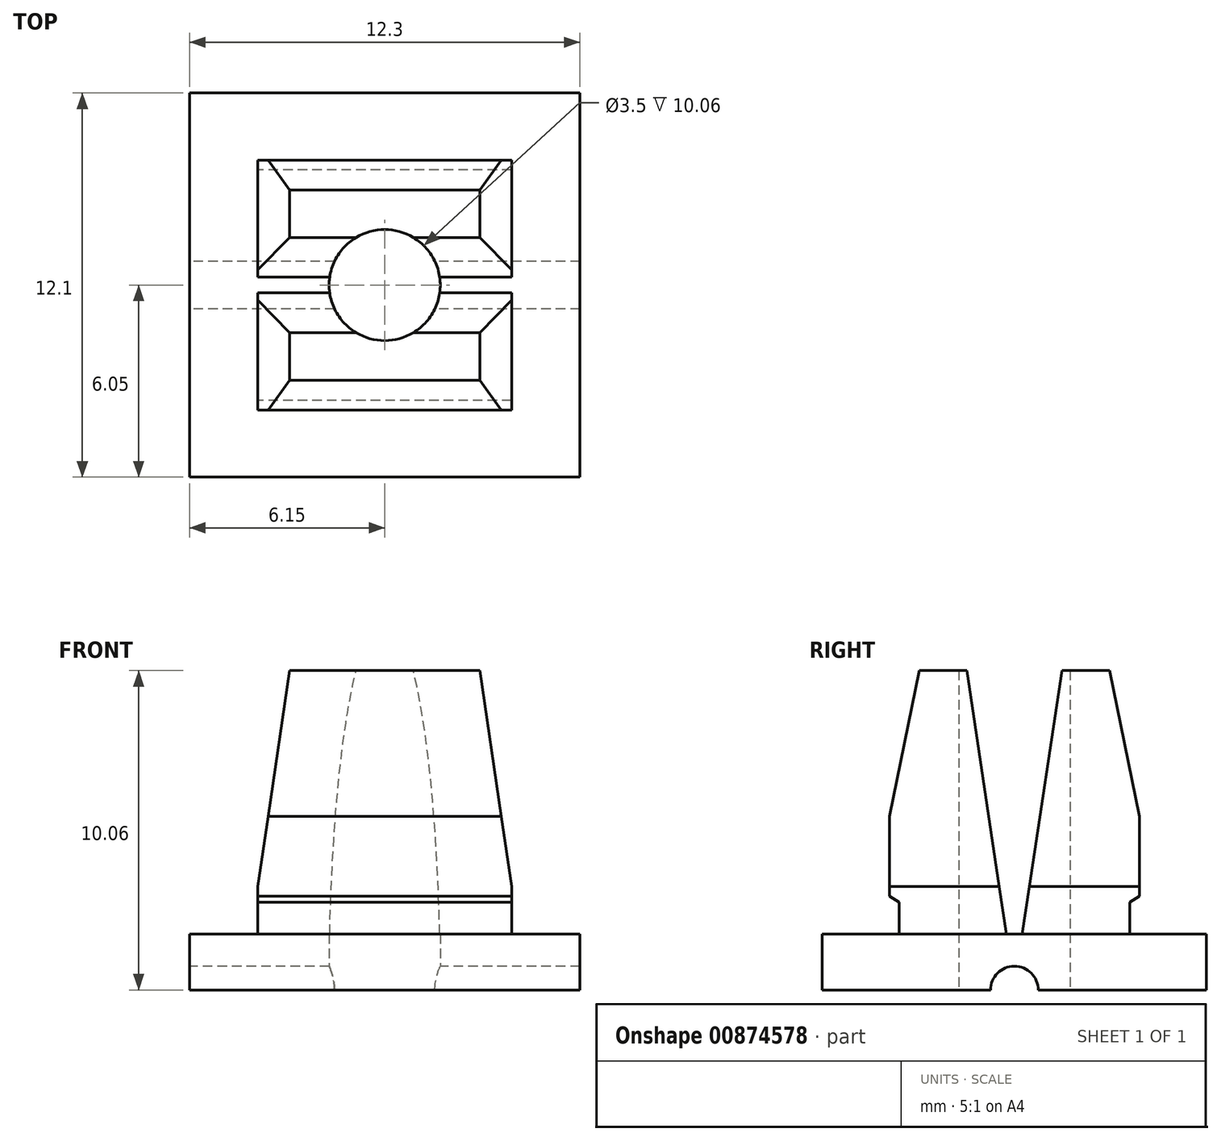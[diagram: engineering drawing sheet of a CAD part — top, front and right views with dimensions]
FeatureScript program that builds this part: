
annotation { "Feature Type Name" : "Feature", "Feature Type Description" : "" }
export const myFeature = defineFeature(function(context is Context, id is Id, definition is map)
    precondition{}
    {
        {
            var Q0;
            Q0=qCreatedBy(makeId("Top.planeOp"),FACE);
            var sketch = newSketch(context, id + "F0", { "sketchPlane" : qUnion([Q0])});
            skLineSegment(sketch, "E0.bottom", {"start": v(-12.3, 12.1) * mm, "end": v(0, 12.1) * mm});
            skLineSegment(sketch, "E0.top", {"start": v(-12.3, 0) * mm, "end": v(0, 0) * mm});
            skLineSegment(sketch, "E0.left", {"start": v(-12.3, 12.1) * mm, "end": v(-12.3, 0) * mm});
            skLineSegment(sketch, "E0.right", {"start": v(0, 12.1) * mm, "end": v(0, 0) * mm});
            skSolve(sketch);
        }
        {
            var Q0;
            Q0=makeQuery(id+"F0.imprint","IMPRINT",FACE,{"disambiguationData":[TD([[makeQuery(id+"F0.imprint","IMPRINT",EDGE,{"derivedFrom":sQuery(id+"F0.wireOp",EDGE,"E0.bottom")}),-1.0]])]});
            extrude(context, id + "F1", {"entities" : qUnion([Q0]), "depth" : 1.76 * mm, "offsetDistance" : 25 * mm});
        }
        {
            var Q0;
            Q0=makeQuery(id+"F1.opExtrude","CAP_FACE",FACE,{"disambiguationData":[OSD([sQuery(id+"F0.wireOp",EDGE,"E0.bottom"),sQuery(id+"F0.wireOp",EDGE,"E0.top"),sQuery(id+"F0.wireOp",EDGE,"E0.left"),sQuery(id+"F0.wireOp",EDGE,"E0.right")])],"isStart":false});
            var sketch = newSketch(context, id + "F2", { "sketchPlane" : qUnion([Q0])});
            skLineSegment(sketch, "E1", {"start": v(-12.3, 0) * mm, "end": v(0, 12.1) * mm, "construction": true});
            skLineSegment(sketch, "E2.bottom", {"start": v(-2.15, 9.98) * mm, "end": v(-10.15, 9.98) * mm});
            skLineSegment(sketch, "E2.top", {"start": v(-2.15, 2.12) * mm, "end": v(-10.15, 2.12) * mm});
            skLineSegment(sketch, "E2.left", {"start": v(-2.15, 9.98) * mm, "end": v(-2.15, 2.12) * mm});
            skLineSegment(sketch, "E2.right", {"start": v(-10.15, 9.98) * mm, "end": v(-10.15, 2.12) * mm});
            skLineSegment(sketch, "E3", {"start": v(-12.3, 12.1) * mm, "end": v(0, 0) * mm, "construction": true});
            skLineSegment(sketch, "E4.bottom", {"start": v(-10.15, 9.98) * mm, "end": v(-2.15, 9.98) * mm});
            skLineSegment(sketch, "E4.top", {"start": v(-10.15, 10.43) * mm, "end": v(-2.15, 10.43) * mm});
            skLineSegment(sketch, "E4.left", {"start": v(-10.15, 9.98) * mm, "end": v(-10.15, 10.43) * mm});
            skLineSegment(sketch, "E4.right", {"start": v(-2.15, 9.98) * mm, "end": v(-2.15, 10.43) * mm});
            skLineSegment(sketch, "E5.bottom", {"start": v(-10.15, 2.12) * mm, "end": v(-2.15, 2.12) * mm});
            skLineSegment(sketch, "E5.top", {"start": v(-10.15, 1.67) * mm, "end": v(-2.15, 1.67) * mm});
            skLineSegment(sketch, "E5.left", {"start": v(-10.15, 2.12) * mm, "end": v(-10.15, 1.67) * mm});
            skLineSegment(sketch, "E5.right", {"start": v(-2.15, 2.12) * mm, "end": v(-2.15, 1.67) * mm});
            skSolve(sketch);
        }
        {
            var Q0;
            Q0=makeQuery(id+"F2.imprint","IMPRINT",FACE,{"disambiguationData":[TD([[makeQuery(id+"F2.imprint","IMPRINT",EDGE,{"derivedFrom":sQuery(id+"F2.wireOp",EDGE,"E4.bottom")}),1.0]])]});
            var Q1;
            Q1=makeQuery(id+"F2.imprint","IMPRINT",FACE,{"disambiguationData":[TD([[makeQuery(id+"F2.imprint","IMPRINT",EDGE,{"derivedFrom":sQuery(id+"F2.wireOp",EDGE,"E2.left")}),-1.0]])]});
            var Q2;
            Q2=makeQuery(id+"F2.imprint","IMPRINT",FACE,{"disambiguationData":[TD([[makeQuery(id+"F2.imprint","IMPRINT",EDGE,{"derivedFrom":sQuery(id+"F2.wireOp",EDGE,"E5.bottom")}),-1.0]])]});
            extrude(context, id + "F3", {"entities" : qUnion([Q0, Q1, Q2]), "operationType" : NewBodyOperationType.ADD, "depth" : 8.3 * mm, "offsetDistance" : 25 * mm});
        }
        {
            var Q0;
            Q0=makeQuery(id+"F3.opExtrude","SWEPT_FACE",FACE,{"disambiguationData":[OSD([sQuery(id+"F2.wireOp",EDGE,"E2.right"),sQuery(id+"F2.wireOp",EDGE,"E4.left"),sQuery(id+"F2.wireOp",EDGE,"E5.left")])]});
            var sketch = newSketch(context, id + "F4", { "sketchPlane" : qUnion([Q0])});
            skLineSegment(sketch, "E6", {"start": v(-7.55, 10.06) * mm, "end": v(-6.3, 1.76) * mm});
            skLineSegment(sketch, "E7", {"start": v(-5.8, 1.76) * mm, "end": v(-4.55, 10.06) * mm});
            skLineSegment(sketch, "E8", {"start": v(-10.43, 3.26) * mm, "end": v(-9.05, 10.06) * mm});
            skLineSegment(sketch, "E9", {"start": v(-1.67, 3.26) * mm, "end": v(-3.05, 10.06) * mm});
            skLineSegment(sketch, "E10", {"start": v(-10.43, 3.26) * mm, "end": v(-9.68, 2.76) * mm});
            skLineSegment(sketch, "E11", {"start": v(-9.68, 2.76) * mm, "end": v(-9.68, 1.76) * mm});
            skLineSegment(sketch, "E12", {"start": v(-1.67, 3.26) * mm, "end": v(-2.42, 2.76) * mm});
            skLineSegment(sketch, "E13", {"start": v(-2.42, 2.76) * mm, "end": v(-2.42, 1.76) * mm});
            skLineSegment(sketch, "E14", {"start": v(-5.8, 1.76) * mm, "end": v(-6.3, 1.76) * mm});
            skSolve(sketch);
        }
        {
            var Q0;
            {var subQ0=sQuery(id+"F4.wireOp",EDGE,"E8");Q0=makeQuery(id+"F4.imprint","IMPRINT",FACE,{"disambiguationData":[TD([[makeQuery(id+"F4.imprint","IMPRINT",EDGE,{"derivedFrom":subQ0}),1.0]])]});}
            var Q1;
            {var subQ0=sQuery(id+"F4.wireOp",EDGE,"E6");Q1=makeQuery(id+"F4.imprint","IMPRINT",FACE,{"disambiguationData":[TD([[makeQuery(id+"F4.imprint","IMPRINT",EDGE,{"derivedFrom":subQ0}),1.0]])]});}
            var Q2;
            {var subQ0=sQuery(id+"F4.wireOp",EDGE,"E9");Q2=makeQuery(id+"F4.imprint","IMPRINT",FACE,{"disambiguationData":[TD([[makeQuery(id+"F4.imprint","IMPRINT",EDGE,{"derivedFrom":subQ0}),-1.0]])]});}
            var Q3;
            {var subQ0=sQuery(id+"F4.wireOp",EDGE,"E10");Q3=makeQuery(id+"F4.imprint","IMPRINT",FACE,{"disambiguationData":[TD([[makeQuery(id+"F4.imprint","IMPRINT",EDGE,{"derivedFrom":subQ0}),-1.0]])]});}
            var Q4;
            {var subQ0=sQuery(id+"F4.wireOp",EDGE,"E12");Q4=makeQuery(id+"F4.imprint","IMPRINT",FACE,{"disambiguationData":[TD([[makeQuery(id+"F4.imprint","IMPRINT",EDGE,{"derivedFrom":subQ0}),1.0]])]});}
            extrude(context, id + "F5", {"entities" : qUnion([Q0, Q1, Q2, Q3, Q4]), "operationType" : NewBodyOperationType.REMOVE, "endBound" : BoundingType.THROUGH_ALL, "oppositeDirection" : true, "depth" : 25 * mm, "offsetDistance" : 25 * mm});
        }
        {
            var Q0;
            Q0=qCreatedBy(makeId("Front.planeOp"),FACE);
            var sketch = newSketch(context, id + "F6", { "sketchPlane" : qUnion([Q0])});
            skLineSegment(sketch, "E15.0", {"start": v(-2.15, 10.06) * mm, "end": v(-10.15, 10.06) * mm, "construction": true});
            skLineSegment(sketch, "E16.0", {"start": v(-10.15, 3.26) * mm, "end": v(-10.15, 10.06) * mm});
            skLineSegment(sketch, "E17.0", {"start": v(-2.15, 3.26) * mm, "end": v(-2.15, 10.06) * mm});
            skLineSegment(sketch, "E18", {"start": v(-9.15, 10.06) * mm, "end": v(-10.15, 3.26) * mm});
            skLineSegment(sketch, "E19", {"start": v(-3.15, 10.06) * mm, "end": v(-2.15, 3.26) * mm});
            skPoint(sketch, "E20", {"position": v(-6.15, 10.06) * mm});
            skLineSegment(sketch, "E21", {"start": v(-10.15, 10.06) * mm, "end": v(-9.15, 10.06) * mm});
            skLineSegment(sketch, "E22", {"start": v(-3.15, 10.06) * mm, "end": v(-2.15, 10.06) * mm});
            skSolve(sketch);
        }
        {
            var Q0;
            Q0=makeQuery(id+"F6.imprint","IMPRINT",FACE,{"disambiguationData":[TD([[makeQuery(id+"F6.imprint","IMPRINT",EDGE,{"derivedFrom":sQuery(id+"F6.wireOp",EDGE,"E16.0")}),-1.0]])]});
            var Q1;
            Q1=makeQuery(id+"F6.imprint","IMPRINT",FACE,{"disambiguationData":[TD([[makeQuery(id+"F6.imprint","IMPRINT",EDGE,{"derivedFrom":sQuery(id+"F6.wireOp",EDGE,"E17.0")}),1.0]])]});
            extrude(context, id + "F7", {"entities" : qUnion([Q0, Q1]), "operationType" : NewBodyOperationType.REMOVE, "endBound" : BoundingType.THROUGH_ALL, "oppositeDirection" : true, "depth" : 25 * mm, "offsetDistance" : 25 * mm});
        }
        {
            var Q0;
            Q0=makeQuery(id+"F1.opExtrude","SWEPT_FACE",FACE,{"disambiguationData":[OSD([sQuery(id+"F0.wireOp",EDGE,"E0.left")])]});
            var sketch = newSketch(context, id + "F8", { "sketchPlane" : qUnion([Q0])});
            skCircle(sketch, "E23", {"center": v(-6.05, 0) * mm, "radius": 0.75 * mm});
            skSolve(sketch);
        }
        {
            var Q0;
            {var subQ0=sQuery(id+"F8.wireOp",EDGE,"E23");var subQ1=makeQuery(id+"F1.opExtrude","CAP_EDGE",EDGE,{"disambiguationData":[OSD([sQuery(id+"F0.wireOp",EDGE,"E0.left")])],"isStart":true});var subQ2=makeQuery(id+"F8.imprint","INTERSECT",VERTEX,{"disambiguationData":[OD(0.0)],"derivedFrom":[subQ1,subQ0]});Q0=makeQuery(id+"F8.imprint","IMPRINT",FACE,{"disambiguationData":[TD([[makeQuery(id+"F8.imprint","IMPRINT",EDGE,{"disambiguationData":[TD([[subQ2,-1.0]])],"derivedFrom":subQ0}),1.0]])]});}
            var Q1;
            {var subQ0=sQuery(id+"F8.wireOp",EDGE,"E23");var subQ1=makeQuery(id+"F1.opExtrude","CAP_EDGE",EDGE,{"disambiguationData":[OSD([sQuery(id+"F0.wireOp",EDGE,"E0.left")])],"isStart":true});var subQ2=makeQuery(id+"F8.imprint","INTERSECT",VERTEX,{"disambiguationData":[OD(0.0)],"derivedFrom":[subQ1,subQ0]});Q1=makeQuery(id+"F8.imprint","IMPRINT",FACE,{"disambiguationData":[TD([[makeQuery(id+"F8.imprint","IMPRINT",EDGE,{"disambiguationData":[TD([[subQ2,1.0]])],"derivedFrom":subQ0}),1.0]])]});}
            extrude(context, id + "F9", {"entities" : qUnion([Q0, Q1]), "operationType" : NewBodyOperationType.REMOVE, "endBound" : BoundingType.THROUGH_ALL, "oppositeDirection" : true, "depth" : 25 * mm, "offsetDistance" : 25 * mm});
        }
        {
            var Q0;
            {var subQ0=sQuery(id+"F0.wireOp",EDGE,"E0.top");var subQ1=sQuery(id+"F0.wireOp",EDGE,"E0.left");var subQ2=sQuery(id+"F0.wireOp",EDGE,"E0.right");Q0=makeQuery(id+"F9.boolean.opBoolean","SPLIT",FACE,{"disambiguationData":[TD([makeQuery(id+"F1.opExtrude","SWEPT_FACE",FACE,{"disambiguationData":[OSD([subQ0])]})])],"derivedFrom":makeQuery(id+"F1.opExtrude","CAP_FACE",FACE,{"disambiguationData":[OSD([sQuery(id+"F0.wireOp",EDGE,"E0.bottom"),subQ0,subQ1,subQ2])],"isStart":true})});}
            var sketch = newSketch(context, id + "F10", { "sketchPlane" : qUnion([Q0])});
            skPoint(sketch, "E24.0", {"position": v(-12.3, -12.1) * mm});
            skPoint(sketch, "E25.0", {"position": v(0, -12.1) * mm});
            skPoint(sketch, "E26.0", {"position": v(-12.3, 0) * mm});
            skLineSegment(sketch, "E27", {"start": v(-12.3, 0) * mm, "end": v(0, -12.1) * mm, "construction": true});
            skLineSegment(sketch, "E28", {"start": v(-12.3, -12.1) * mm, "end": v(0, 0) * mm, "construction": true});
            skCircle(sketch, "E29", {"center": v(-6.15, -6.05) * mm, "radius": 1.75 * mm});
            skSolve(sketch);
        }
        {
            var Q0;
            {var subQ0=sQuery(id+"F10.wireOp",EDGE,"E29");var subQ1=makeQuery(id+"F9.boolean.opBoolean","INTERSECT",EDGE,{"disambiguationData":[OD(1.0)],"derivedFrom":[makeQuery(id+"F1.opExtrude","CAP_FACE",FACE,{"disambiguationData":[OSD([sQuery(id+"F0.wireOp",EDGE,"E0.bottom"),sQuery(id+"F0.wireOp",EDGE,"E0.top"),sQuery(id+"F0.wireOp",EDGE,"E0.left"),sQuery(id+"F0.wireOp",EDGE,"E0.right")])],"isStart":true}),makeQuery(id+"F9.opExtrude","SWEPT_FACE",FACE,{"disambiguationData":[OSD([sQuery(id+"F8.wireOp",EDGE,"E23")])]})]});var subQ2=makeQuery(id+"F10.imprint","INTERSECT",VERTEX,{"disambiguationData":[OD(0.0)],"derivedFrom":[subQ1,subQ0]});Q0=makeQuery(id+"F10.imprint","IMPRINT",FACE,{"disambiguationData":[TD([[makeQuery(id+"F10.imprint","IMPRINT",EDGE,{"disambiguationData":[TD([[subQ2,1.0]])],"derivedFrom":subQ0}),1.0]])]});}
            var Q1;
            {var subQ0=sQuery(id+"F10.wireOp",EDGE,"E29");var subQ1=makeQuery(id+"F9.boolean.opBoolean","INTERSECT",EDGE,{"disambiguationData":[OD(1.0)],"derivedFrom":[makeQuery(id+"F1.opExtrude","CAP_FACE",FACE,{"disambiguationData":[OSD([sQuery(id+"F0.wireOp",EDGE,"E0.bottom"),sQuery(id+"F0.wireOp",EDGE,"E0.top"),sQuery(id+"F0.wireOp",EDGE,"E0.left"),sQuery(id+"F0.wireOp",EDGE,"E0.right")])],"isStart":true}),makeQuery(id+"F9.opExtrude","SWEPT_FACE",FACE,{"disambiguationData":[OSD([sQuery(id+"F8.wireOp",EDGE,"E23")])]})]});var subQ2=makeQuery(id+"F10.imprint","INTERSECT",VERTEX,{"disambiguationData":[OD(0.0)],"derivedFrom":[subQ1,subQ0]});Q1=makeQuery(id+"F10.imprint","IMPRINT",FACE,{"disambiguationData":[TD([[makeQuery(id+"F10.imprint","IMPRINT",EDGE,{"disambiguationData":[TD([[subQ2,-1.0]])],"derivedFrom":subQ0}),1.0]])]});}
            extrude(context, id + "F11", {"entities" : qUnion([Q0, Q1]), "operationType" : NewBodyOperationType.REMOVE, "endBound" : BoundingType.THROUGH_ALL, "oppositeDirection" : true, "depth" : 25 * mm, "offsetDistance" : 25 * mm});
        }
    });
